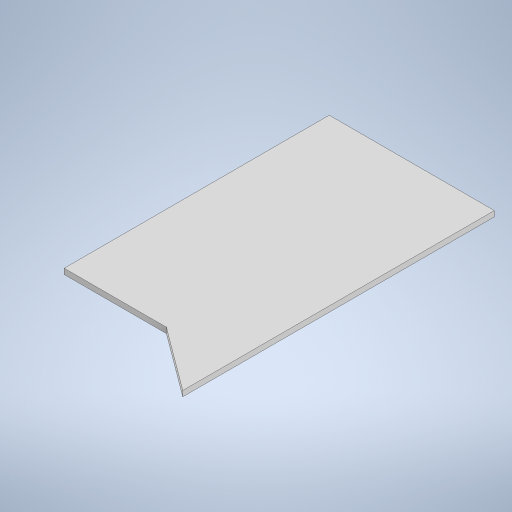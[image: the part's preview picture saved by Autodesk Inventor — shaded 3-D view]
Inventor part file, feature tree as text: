
AUTODESK INVENTOR PART (.ipt)
format: ipt  version: 2024 (Build 280153000, 153)  size: 531,968 bytes
history: native  units: mm
features: extrude x2, sketch x2
ambient origin geometry x8: Origin, YZ Plane, XZ Plane, XY Plane, X Axis, Y Axis, Z Axis, Center Point
bodies: Solid1 (feature_tree)
feature tree (4):
  extrude  "Extrusion1"  Depth=60.0mm
  extrude  "Extrusion2"  Depth=37.0mm
  sketch  "Sketch1"  dims[d0=113.2mm d2=60.0mm]
  sketch  "Sketch2"  dims[d3=2.0mm d4=0.0mm d5=9.337511mm d6=37.0mm d7=0.1mm d8=0.0mm]
